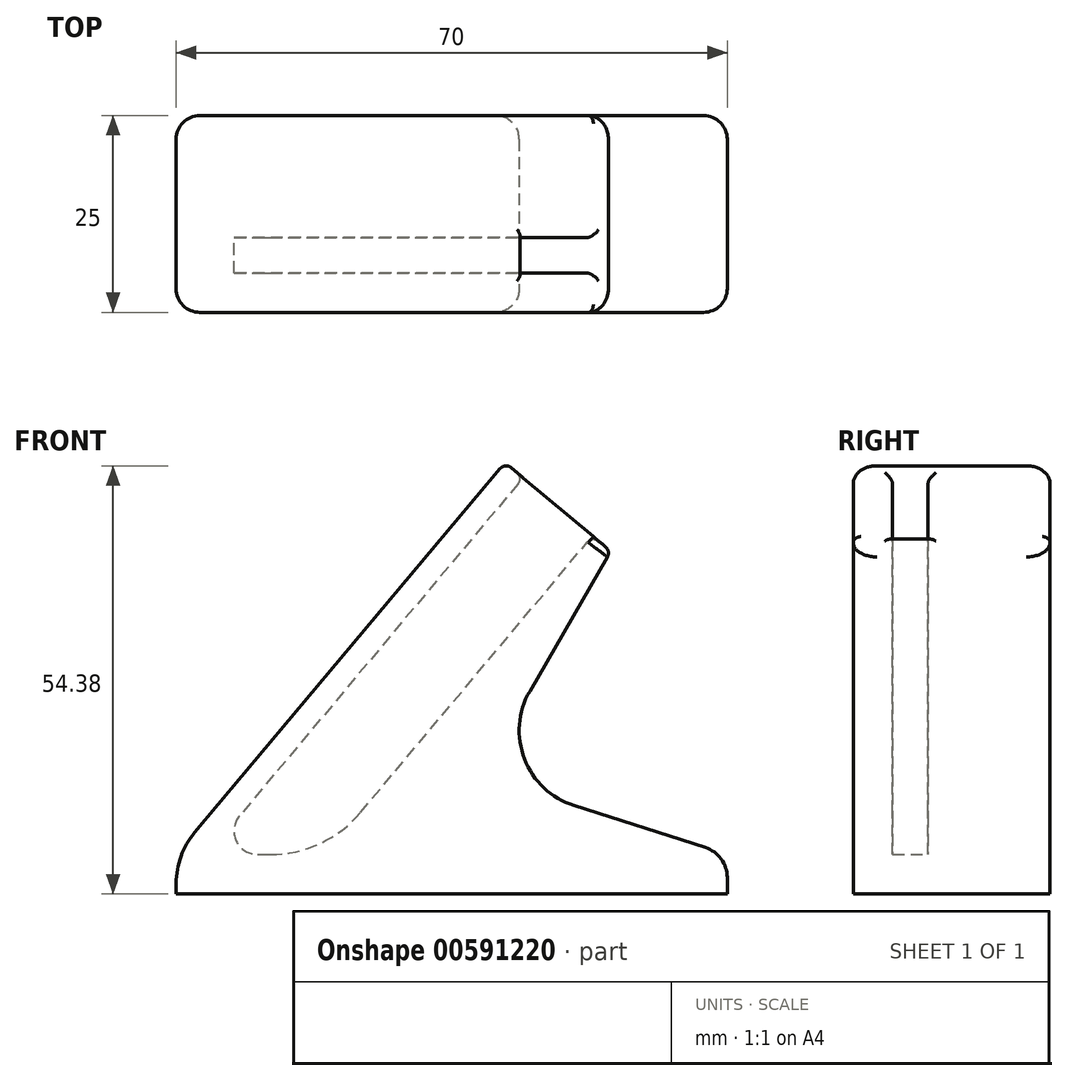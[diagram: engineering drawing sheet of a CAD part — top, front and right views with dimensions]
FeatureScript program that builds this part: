
annotation { "Feature Type Name" : "Feature", "Feature Type Description" : "" }
export const myFeature = defineFeature(function(context is Context, id is Id, definition is map)
    precondition{}
    {
        {
            var Q0;
            Q0=qCreatedBy(makeId("Front.planeOp"),FACE);
            var sketch = newSketch(context, id + "F0", { "sketchPlane" : qUnion([Q0])});
            skLineSegment(sketch, "E0", {"start": v(0, 0) * mm, "end": v(0, 5) * mm});
            skLineSegment(sketch, "E1", {"start": v(0, 5) * mm, "end": v(41.78, 54.8) * mm});
            skLineSegment(sketch, "E2", {"start": v(41.78, 54.8) * mm, "end": v(55.19, 43.54) * mm});
            skLineSegment(sketch, "E3", {"start": v(55.19, 43.54) * mm, "end": v(38.7, 15) * mm});
            skLineSegment(sketch, "E4", {"start": v(38.7, 15) * mm, "end": v(70, 5) * mm});
            skLineSegment(sketch, "E5", {"start": v(70, 5) * mm, "end": v(70, 0) * mm});
            skLineSegment(sketch, "E6", {"start": v(70, 0) * mm, "end": v(0, 0) * mm});
            skSolve(sketch);
        }
        {
            var Q0;
            Q0 = qSketchRegion(id + "F0", true);
            extrude(context, id + "F1", {"entities" : qUnion([Q0]), "depth" : 12.5 * mm, "offsetDistance" : 25 * mm, "hasSecondDirection" : true, "secondDirectionOppositeDirection" : true, "secondDirectionDepth" : 12.5 * mm});
        }
        {
            var Q0;
            Q0=qCreatedBy(makeId("Front.planeOp"),FACE);
            cPlane(context, id + "F2", {"entities" : qUnion([Q0]), "cplaneType" : CPlaneType.OFFSET, "offset" : 3 * mm, "width" : 150 * mm, "height" : 150 * mm});
        }
        {
            var Q0;
            Q0=qCreatedBy(id+"F2.planeOp",FACE);
            var sketch = newSketch(context, id + "F3", { "sketchPlane" : qUnion([Q0])});
            skLineSegment(sketch, "E7", {"start": v(44.08, 52.86) * mm, "end": v(8.05, 9.93) * mm});
            skLineSegment(sketch, "E8", {"start": v(10.35, 5) * mm, "end": v(11.93, 5) * mm});
            skLineSegment(sketch, "E9", {"start": v(23.42, 10.36) * mm, "end": v(52.89, 45.47) * mm});
            skLineSegment(sketch, "E10", {"start": v(52.89, 45.47) * mm, "end": v(44.08, 52.86) * mm});
            skPoint(sketch, "E11.visualSharp", {"position": v(3.92, 5) * mm});
            skArc(sketch, "E11.filletArc", {"start": v(8.05, 9.93) * mm, "mid": v(7.63, 6.73) * mm, "end": v(10.35, 5) * mm});
            skPoint(sketch, "E12.visualSharp", {"position": v(18.93, 5) * mm});
            skArc(sketch, "E12.filletArc", {"start": v(11.93, 5) * mm, "mid": v(18.27, 6.4) * mm, "end": v(23.42, 10.36) * mm});
            skSolve(sketch);
        }
        {
            var Q0;
            Q0 = qSketchRegion(id + "F3", true);
            extrude(context, id + "F4", {"entities" : qUnion([Q0]), "operationType" : NewBodyOperationType.REMOVE, "depth" : 4.5 * mm, "offsetDistance" : 25 * mm});
        }
        {
            var Q0;
            Q0=makeQuery(id+"F1.opExtrude","SWEPT_EDGE",EDGE,{"disambiguationData":[OSD([sQuery(id+"F0.wireOp",EDGE,"E3"),sQuery(id+"F0.wireOp",EDGE,"E4")])]});
            var Q1;
            Q1=makeQuery(id+"F1.opExtrude","SWEPT_EDGE",EDGE,{"disambiguationData":[OSD([sQuery(id+"F0.wireOp",EDGE,"E0"),sQuery(id+"F0.wireOp",EDGE,"E1")])]});
            fillet(context, id + "F5", {"entities" : qUnion([Q0, Q1]), "radius" : 10 * mm, "tangentPropagation" : true, "allowEdgeOverflow" : false});
        }
        {
            var Q0;
            Q0=makeQuery(id+"F1.opExtrude","SWEPT_EDGE",EDGE,{"disambiguationData":[OSD([sQuery(id+"F0.wireOp",EDGE,"E4"),sQuery(id+"F0.wireOp",EDGE,"E5")])]});
            fillet(context, id + "F6", {"entities" : qUnion([Q0]), "radius" : 4 * mm, "tangentPropagation" : true, "allowEdgeOverflow" : false});
        }
        {
            var Q0;
            Q0=makeQuery(id+"F1.opExtrude","CAP_EDGE",EDGE,{"disambiguationData":[OSD([sQuery(id+"F0.wireOp",EDGE,"E1")])],"isStart":false});
            var Q1;
            Q1=makeQuery(id+"F1.opExtrude","CAP_EDGE",EDGE,{"disambiguationData":[OSD([sQuery(id+"F0.wireOp",EDGE,"E3")])],"isStart":false});
            var Q2;
            Q2=makeQuery(id+"F1.opExtrude","CAP_EDGE",EDGE,{"disambiguationData":[OSD([sQuery(id+"F0.wireOp",EDGE,"E3")])],"isStart":true});
            var Q3;
            Q3=makeQuery(id+"F1.opExtrude","CAP_EDGE",EDGE,{"disambiguationData":[OSD([sQuery(id+"F0.wireOp",EDGE,"E1")])],"isStart":true});
            fillet(context, id + "F7", {"entities" : qUnion([Q0, Q1, Q2, Q3]), "radius" : 3 * mm, "tangentPropagation" : true, "allowEdgeOverflow" : false});
        }
        {
            var Q0;
            Q0=makeQuery(id+"F1.opExtrude","SWEPT_FACE",FACE,{"disambiguationData":[OSD([sQuery(id+"F0.wireOp",EDGE,"E2")])]});
            fillet(context, id + "F8", {"entities" : qUnion([Q0]), "radius" : 1 * mm, "tangentPropagation" : true, "allowEdgeOverflow" : false});
        }
    });
